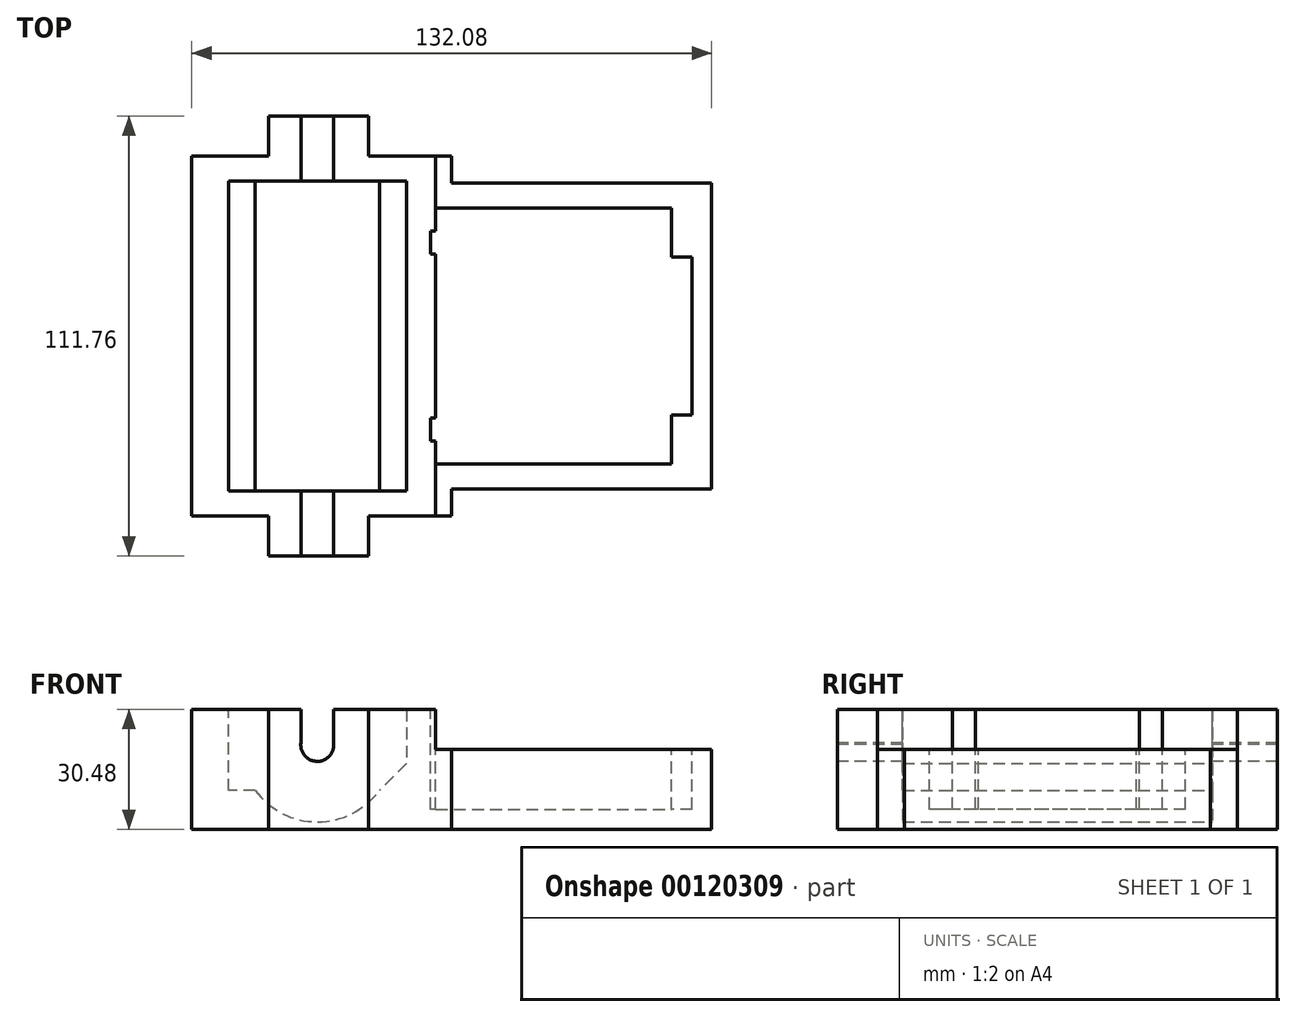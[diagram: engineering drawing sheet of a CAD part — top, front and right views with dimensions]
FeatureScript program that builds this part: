
annotation { "Feature Type Name" : "Feature", "Feature Type Description" : "" }
export const myFeature = defineFeature(function(context is Context, id is Id, definition is map)
    precondition{}
    {
        {
            var Q0;
            Q0=qCreatedBy(makeId("Top.planeOp"),FACE);
            var sketch = newSketch(context, id + "F0", { "sketchPlane" : qUnion([Q0])});
            skLineSegment(sketch, "E0.bottom", {"start": v(-66.04, 55.88) * mm, "end": v(66.04, 55.88) * mm});
            skLineSegment(sketch, "E0.top", {"start": v(-66.04, -55.88) * mm, "end": v(66.04, -55.88) * mm});
            skLineSegment(sketch, "E0.left", {"start": v(-66.04, 55.88) * mm, "end": v(-66.04, -55.88) * mm});
            skLineSegment(sketch, "E0.right", {"start": v(66.04, 55.88) * mm, "end": v(66.04, -55.88) * mm});
            skSolve(sketch);
        }
        {
            var Q0;
            Q0 = qSketchRegion(id + "F0", true);
            extrude(context, id + "F1", {"entities" : qUnion([Q0]), "depth" : 30.48 * mm});
        }
        {
            var Q0;
            Q0=makeQuery(id+"F1.opExtrude","CAP_FACE",FACE,{"disambiguationData":[OSD([sQuery(id+"F0.wireOp",EDGE,"E0.bottom"),sQuery(id+"F0.wireOp",EDGE,"E0.top"),sQuery(id+"F0.wireOp",EDGE,"E0.left"),sQuery(id+"F0.wireOp",EDGE,"E0.right")])],"isStart":false});
            var sketch = newSketch(context, id + "F2", { "sketchPlane" : qUnion([Q0])});
            skLineSegment(sketch, "E1.bottom", {"start": v(-4.06, 32.51) * mm, "end": v(55.88, 32.51) * mm});
            skLineSegment(sketch, "E1.top", {"start": v(-4.06, -32.51) * mm, "end": v(55.88, -32.51) * mm});
            skLineSegment(sketch, "E1.left", {"start": v(-4.06, 32.51) * mm, "end": v(-4.06, 26.67) * mm});
            skLineSegment(sketch, "E1.right", {"start": v(55.88, 32.51) * mm, "end": v(55.88, 20.07) * mm});
            skLineSegment(sketch, "E2", {"start": v(55.88, 20.07) * mm, "end": v(61.05, 20.07) * mm});
            skLineSegment(sketch, "E3", {"start": v(61.05, 20.07) * mm, "end": v(61.05, -20.07) * mm});
            skLineSegment(sketch, "E4", {"start": v(61.05, -20.07) * mm, "end": v(55.88, -20.07) * mm});
            skLineSegment(sketch, "E5.trimOffspring", {"start": v(55.88, -20.07) * mm, "end": v(55.88, -32.51) * mm});
            skLineSegment(sketch, "E6", {"start": v(-4.06, 26.67) * mm, "end": v(-5.33, 26.67) * mm});
            skLineSegment(sketch, "E7", {"start": v(-5.33, 26.67) * mm, "end": v(-5.33, 20.83) * mm});
            skLineSegment(sketch, "E8", {"start": v(-5.33, 20.83) * mm, "end": v(-4.06, 20.83) * mm});
            skLineSegment(sketch, "E9", {"start": v(-4.06, -20.83) * mm, "end": v(-5.33, -20.83) * mm});
            skLineSegment(sketch, "E10", {"start": v(-5.33, -20.83) * mm, "end": v(-5.33, -26.67) * mm});
            skLineSegment(sketch, "E11", {"start": v(-5.33, -26.67) * mm, "end": v(-4.06, -26.67) * mm});
            skLineSegment(sketch, "E12.trimOffspring", {"start": v(-4.06, 20.83) * mm, "end": v(-4.06, -20.83) * mm});
            skLineSegment(sketch, "E13.trimOffspring", {"start": v(-4.06, -26.67) * mm, "end": v(-4.06, -32.51) * mm});
            skSolve(sketch);
        }
        {
            var Q0;
            Q0 = qSketchRegion(id + "F2", true);
            extrude(context, id + "F3", {"entities" : qUnion([Q0]), "operationType" : NewBodyOperationType.REMOVE, "oppositeDirection" : true, "depth" : 25.4 * mm});
        }
        {
            var Q0;
            Q0=qCreatedBy(makeId("Front.planeOp"),FACE);
            var sketch = newSketch(context, id + "F4", { "sketchPlane" : qUnion([Q0])});
            skLineSegment(sketch, "E14", {"start": v(-34.16, 15.53) * mm, "end": v(-34.16, 21.48) * mm, "construction": true});
            skArc(sketch, "E15", {"start": v(-49.9, 9.88) * mm, "mid": v(-34.16, 1.92) * mm, "end": v(-18.41, 9.88) * mm});
            skLineSegment(sketch, "E16", {"start": v(-49.9, 9.88) * mm, "end": v(-18.41, 9.88) * mm, "construction": true});
            skLineSegment(sketch, "E17", {"start": v(-49.9, 9.88) * mm, "end": v(-56.77, 9.88) * mm});
            skLineSegment(sketch, "E18", {"start": v(-56.77, 9.88) * mm, "end": v(-56.77, 37.63) * mm});
            skLineSegment(sketch, "E19", {"start": v(-56.77, 37.63) * mm, "end": v(-11.55, 37.63) * mm});
            skLineSegment(sketch, "E20", {"start": v(-11.55, 37.63) * mm, "end": v(-11.55, 16.74) * mm});
            skLineSegment(sketch, "E21", {"start": v(-11.55, 16.74) * mm, "end": v(-18.41, 9.88) * mm});
            skLineSegment(sketch, "E22", {"start": v(-11.55, 16.74) * mm, "end": v(-11.55, 9.88) * mm, "construction": true});
            skLineSegment(sketch, "E23", {"start": v(-11.55, 9.88) * mm, "end": v(-18.41, 9.88) * mm, "construction": true});
            skSolve(sketch);
        }
        {
            var Q0;
            Q0 = qSketchRegion(id + "F4", true);
            extrude(context, id + "F5", {"entities" : qUnion([Q0]), "operationType" : NewBodyOperationType.REMOVE, "depth" : 39.37 * mm, "hasSecondDirection" : true, "secondDirectionOppositeDirection" : true, "secondDirectionDepth" : 39.37 * mm});
        }
        {
            var Q0;
            Q0=qCreatedBy(makeId("Front.planeOp"),FACE);
            var sketch = newSketch(context, id + "F6", { "sketchPlane" : qUnion([Q0])});
            skArc(sketch, "E24", {"start": v(-38.33, 21.94) * mm, "mid": v(-34.35, 17.3) * mm, "end": v(-29.97, 21.57) * mm});
            skLineSegment(sketch, "E25", {"start": v(-29.97, 21.4) * mm, "end": v(-29.97, 31.2) * mm});
            skLineSegment(sketch, "E26", {"start": v(-38.33, 21.94) * mm, "end": v(-38.33, 31.2) * mm});
            skLineSegment(sketch, "E27", {"start": v(-38.33, 31.2) * mm, "end": v(-29.97, 31.2) * mm});
            skSolve(sketch);
        }
        {
            var Q0;
            Q0 = qSketchRegion(id + "F6", true);
            extrude(context, id + "F7", {"entities" : qUnion([Q0]), "operationType" : NewBodyOperationType.REMOVE, "oppositeDirection" : true, "depth" : 127 * mm, "hasSecondDirection" : true, "secondDirectionOppositeDirection" : false, "secondDirectionDepth" : 127 * mm});
        }
        {
            var Q0;
            Q0=makeQuery(id+"F1.opExtrude","SWEPT_FACE",FACE,{"disambiguationData":[OSD([sQuery(id+"F0.wireOp",EDGE,"E0.top")])]});
            var sketch = newSketch(context, id + "F8", { "sketchPlane" : qUnion([Q0])});
            skLineSegment(sketch, "E28.bottom", {"start": v(-4.13, 30.48) * mm, "end": v(66.04, 30.48) * mm});
            skLineSegment(sketch, "E28.top", {"start": v(-4.13, 20.32) * mm, "end": v(66.04, 20.32) * mm});
            skLineSegment(sketch, "E28.left", {"start": v(-4.13, 30.48) * mm, "end": v(-4.13, 20.32) * mm});
            skLineSegment(sketch, "E28.right", {"start": v(66.04, 30.48) * mm, "end": v(66.04, 20.32) * mm});
            skSolve(sketch);
        }
        {
            var Q0;
            Q0 = qSketchRegion(id + "F8", true);
            extrude(context, id + "F9", {"entities" : qUnion([Q0]), "operationType" : NewBodyOperationType.REMOVE, "oppositeDirection" : true, "depth" : 124.52 * mm});
        }
        {
            var Q0;
            {var subQ6=sQuery(id+"F0.wireOp",EDGE,"E0.left");var subQ7=sQuery(id+"F0.wireOp",EDGE,"E0.top");var subQ8=sQuery(id+"F0.wireOp",EDGE,"E0.bottom");Q0=makeQuery(id+"F7.boolean.opBoolean","SPLIT",FACE,{"disambiguationData":[TD([makeQuery(id+"F1.opExtrude","SWEPT_FACE",FACE,{"disambiguationData":[OSD([subQ6])]})])],"derivedFrom":makeQuery(id+"F1.opExtrude","CAP_FACE",FACE,{"disambiguationData":[OSD([subQ8,subQ7,subQ6,sQuery(id+"F0.wireOp",EDGE,"E0.right")])],"isStart":false})});}
            var sketch = newSketch(context, id + "F10", { "sketchPlane" : qUnion([Q0])});
            skLineSegment(sketch, "E29", {"start": v(-66.04, 45.72) * mm, "end": v(-46.48, 45.72) * mm});
            skLineSegment(sketch, "E30", {"start": v(-46.48, 45.72) * mm, "end": v(-46.48, 60.96) * mm});
            skLineSegment(sketch, "E31", {"start": v(-46.48, 60.96) * mm, "end": v(-21.08, 60.96) * mm});
            skLineSegment(sketch, "E32", {"start": v(-21.08, 60.96) * mm, "end": v(-21.08, 45.72) * mm});
            skLineSegment(sketch, "E33", {"start": v(-21.08, 45.72) * mm, "end": v(0, 45.72) * mm});
            skLineSegment(sketch, "E34", {"start": v(0, 45.72) * mm, "end": v(0, 38.86) * mm});
            skLineSegment(sketch, "E35", {"start": v(0, 38.86) * mm, "end": v(67.55, 38.86) * mm});
            skLineSegment(sketch, "E36", {"start": v(67.55, 38.86) * mm, "end": v(67.55, -38.86) * mm});
            skLineSegment(sketch, "E37", {"start": v(67.55, -38.86) * mm, "end": v(0, -38.86) * mm});
            skLineSegment(sketch, "E38", {"start": v(0, -38.86) * mm, "end": v(0, -45.72) * mm});
            skLineSegment(sketch, "E39", {"start": v(0, -45.72) * mm, "end": v(-21.08, -45.72) * mm});
            skLineSegment(sketch, "E40", {"start": v(-21.08, -45.72) * mm, "end": v(-21.08, -60.96) * mm});
            skLineSegment(sketch, "E41", {"start": v(-21.08, -60.96) * mm, "end": v(-46.48, -60.96) * mm});
            skLineSegment(sketch, "E42", {"start": v(-46.48, -60.96) * mm, "end": v(-46.48, -45.72) * mm});
            skLineSegment(sketch, "E43", {"start": v(-46.48, -45.72) * mm, "end": v(-66.04, -45.72) * mm});
            skLineSegment(sketch, "E44", {"start": v(-66.04, -45.72) * mm, "end": v(-66.04, 45.72) * mm});
            skLineSegment(sketch, "E45.bottom", {"start": v(-108.6, 91.7) * mm, "end": v(110.43, 91.7) * mm});
            skLineSegment(sketch, "E45.top", {"start": v(-108.6, -99.7) * mm, "end": v(110.43, -99.7) * mm});
            skLineSegment(sketch, "E45.left", {"start": v(-108.6, 91.7) * mm, "end": v(-108.6, -99.7) * mm});
            skLineSegment(sketch, "E45.right", {"start": v(110.43, 91.7) * mm, "end": v(110.43, -99.7) * mm});
            skSolve(sketch);
        }
        {
            var Q0;
            Q0 = qSketchRegion(id + "F10", true);
            extrude(context, id + "F11", {"entities" : qUnion([Q0]), "operationType" : NewBodyOperationType.REMOVE, "oppositeDirection" : true, "depth" : 40.6 * mm});
        }
    });
